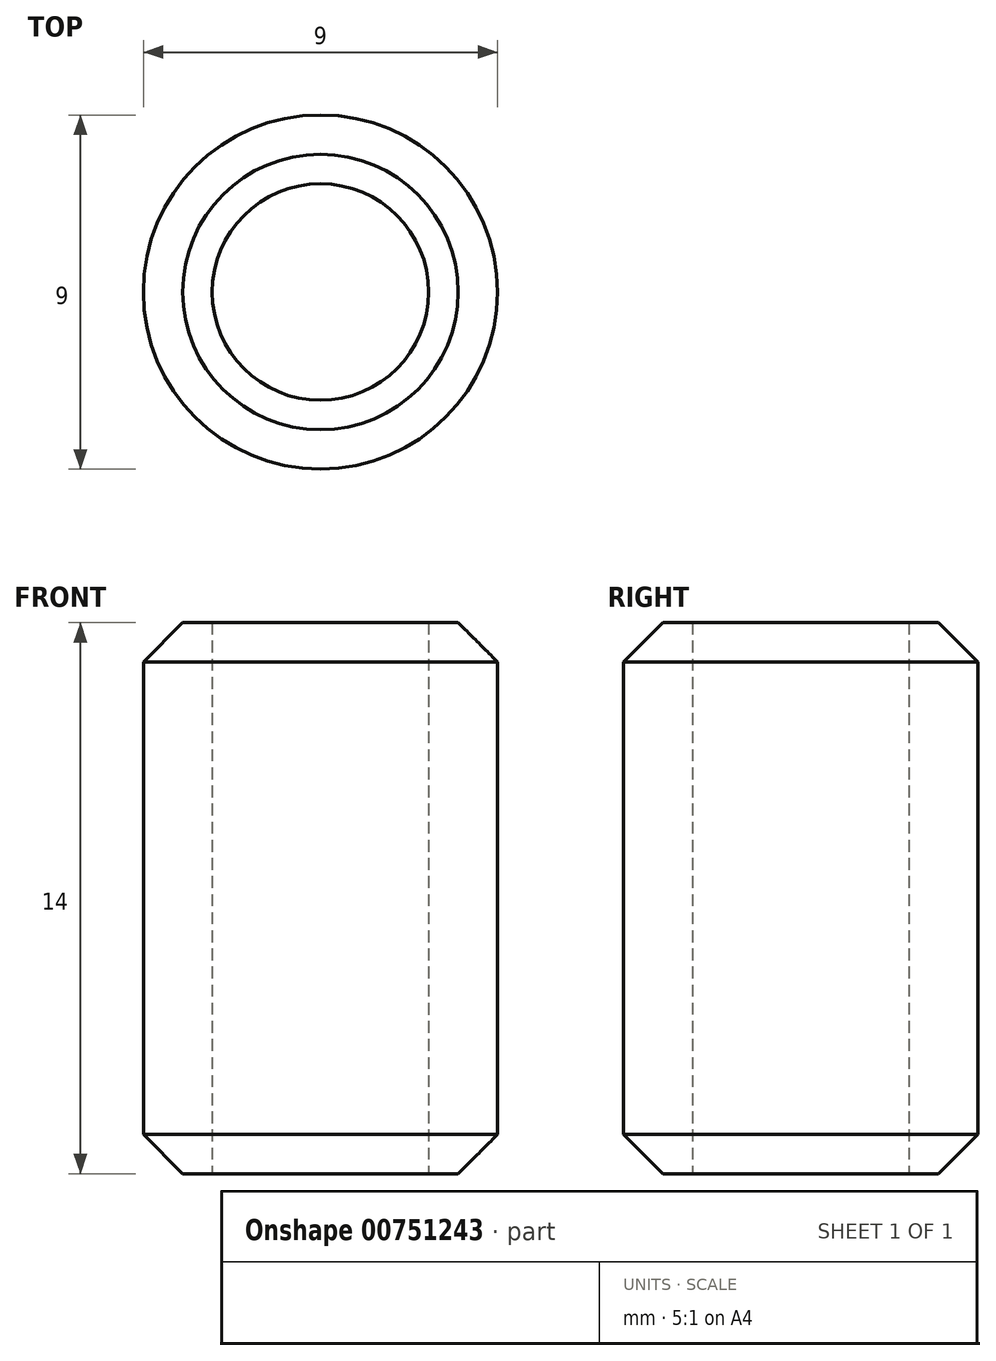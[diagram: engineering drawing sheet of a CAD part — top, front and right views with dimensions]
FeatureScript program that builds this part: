
annotation { "Feature Type Name" : "Feature", "Feature Type Description" : "" }
export const myFeature = defineFeature(function(context is Context, id is Id, definition is map)
    precondition{}
    {
        {
            assignVariable(context, id + "F0", {"name" : "SpacerHeight", "anyValue" : 14});
        }
        {
            var Q0;
            Q0=qCreatedBy(makeId("Top.planeOp"),FACE);
            var sketch = newSketch(context, id + "F1", { "sketchPlane" : qUnion([Q0])});
            skCircle(sketch, "E0", {"center": v(0, 0) * mm, "radius": 2.75 * mm});
            skCircle(sketch, "E1", {"center": v(0, 0) * mm, "radius": 4.5 * mm});
            skSolve(sketch);
        }
        {
            var Q0;
            Q0=makeQuery(id+"F1.imprint","IMPRINT",FACE,{"disambiguationData":[TD([[makeQuery(id+"F1.imprint","IMPRINT",EDGE,{"derivedFrom":sQuery(id+"F1.wireOp",EDGE,"E0")}),-1.0]])]});
            extrude(context, id + "F2", {"entities" : qUnion([Q0]), "depth" : (getVariable(context, 'SpacerHeight')) * mm, "offsetDistance" : 25 * mm});
        }
        {
            var Q0;
            Q0=makeQuery(id+"F2.opExtrude","CAP_EDGE",EDGE,{"disambiguationData":[OSD([sQuery(id+"F1.wireOp",EDGE,"E1")])],"isStart":false});
            var Q1;
            Q1=makeQuery(id+"F2.opExtrude","CAP_EDGE",EDGE,{"disambiguationData":[OSD([sQuery(id+"F1.wireOp",EDGE,"E1")])],"isStart":true});
            chamfer(context, id + "F3", {"entities" : qUnion([Q0, Q1]), "width" : 1 * mm, "tangentPropagation" : true});
        }
    });
